# Revit family: HES
name_source: partatom
category: Mechanical Equipment
units: mm (PartAtom-declared; Revit-internal decimal feet)

## family parameters
Always vertical = Yes
Cut with Voids When Loaded = No
Part Type = Normal
Room Calculation Point = No
Round Connector Dimension = Use Diameter
Shared = No
Work Plane-Based = No

## types (8) — shared parameters
1" = 1 "
1.5 = 1.5 "
2" = 2 "
2' = 24 "
4" = 4 "
B = 3 "
B-.125" = 2.875 "
B/2 = 1.5 "
Manufacturer = Loren Cook Company
Model = HES
ONE EIGTH = 0.125 "
Type Comments = Hooded Supply Ventilator Extruded Aluminum Propeller Roof Mounted/Belt Drive
URL = www.lorencook.com
zero-valued in all types: 0

## per-type parameters (varying)
| type | (A-C)/2 | (T_SQ/2)+.125" | (T_SQ/2)-2" | -(A/2) | -(C/2) | -L/2 | A | A-1.5" | A-C | A/2 | C | C/2 | L | L/2 | RO | RO/2 | T_SQ | T_SQ/2 | W | W/2 |
| 24-HES | 9.375 " | 18.125 " | 16 " | -14.375 " | -5 " | -29.5 " | 28.75 " | 27.25 " | 18.75 " | 14.375 " | 10 " | 5 " | 59 " | 29.5 " | 31.5 " | 15.75 " | 36 " | 18 " | 59 " | 29.5 " |
| 30-HES | 10.25 " | 21.125 " | 19 " | -15.25 " | -5 " | -34.5 " | 30.5 " | 29 " | 20.5 " | 15.25 " | 10 " | 5 " | 69 " | 34.5 " | 37.5 " | 18.75 " | 42 " | 21 " | 69 " | 34.5 " |
| 36-HES | 11.5 " | 24.125 " | 22 " | -16.5 " | -5 " | -40 " | 33 " | 31.5 " | 23 " | 16.5 " | 10 " | 5 " | 80 " | 40 " | 43.5 " | 21.75 " | 48 " | 24 " | 80 " | 40 " |
| 42-HES | 14 " | 27.125 " | 25 " | -19 " | -5 " | -45 " | 38 " | 36.5 " | 28 " | 19 " | 10 " | 5 " | 90 " | 45 " | 49.5 " | 24.75 " | 54 " | 27 " | 90 " | 45 " |
| 48-HES | 14 " | 30.125 " | 28 " | -20.75 " | -6.75 " | -55 " | 41.5 " | 40 " | 28 " | 20.75 " | 13.5 " | 6.75 " | 110 " | 55 " | 55.5 " | 27.75 " | 60 " | 30 " | 90 " | 45 " |
| 54-HES | 14.875 " | 33.125 " | 31 " | -22.25 " | -7.375 " | -55.5 " | 44.5 " | 43 " | 29.75 " | 22.25 " | 14.75 " | 7.375 " | 111 " | 55.5 " | 61.5 " | 30.75 " | 66 " | 33 " | 109 " | 54.5 " |
| 60-HES | 14.875 " | 36.125 " | 34 " | -22.25 " | -7.375 " | -60.5 " | 44.5 " | 43 " | 29.75 " | 22.25 " | 14.75 " | 7.375 " | 121 " | 60.5 " | 67.5 " | 33.75 " | 72 " | 36 " | 119 " | 59.5 " |
| 72-HES | 12.125 " | 42.125 " | 40 " | -21 " | -8.875 " | -73 " | 42 " | 40.5 " | 24.25 " | 21 " | 17.75 " | 8.875 " | 146 " | 73 " | 79.5 " | 39.75 " | 84 " | 42 " | 119 " | 59.5 " |

## geometry (parser evidence)
native form markers: Sweep x2
no freeform markers — native parametric forms only
